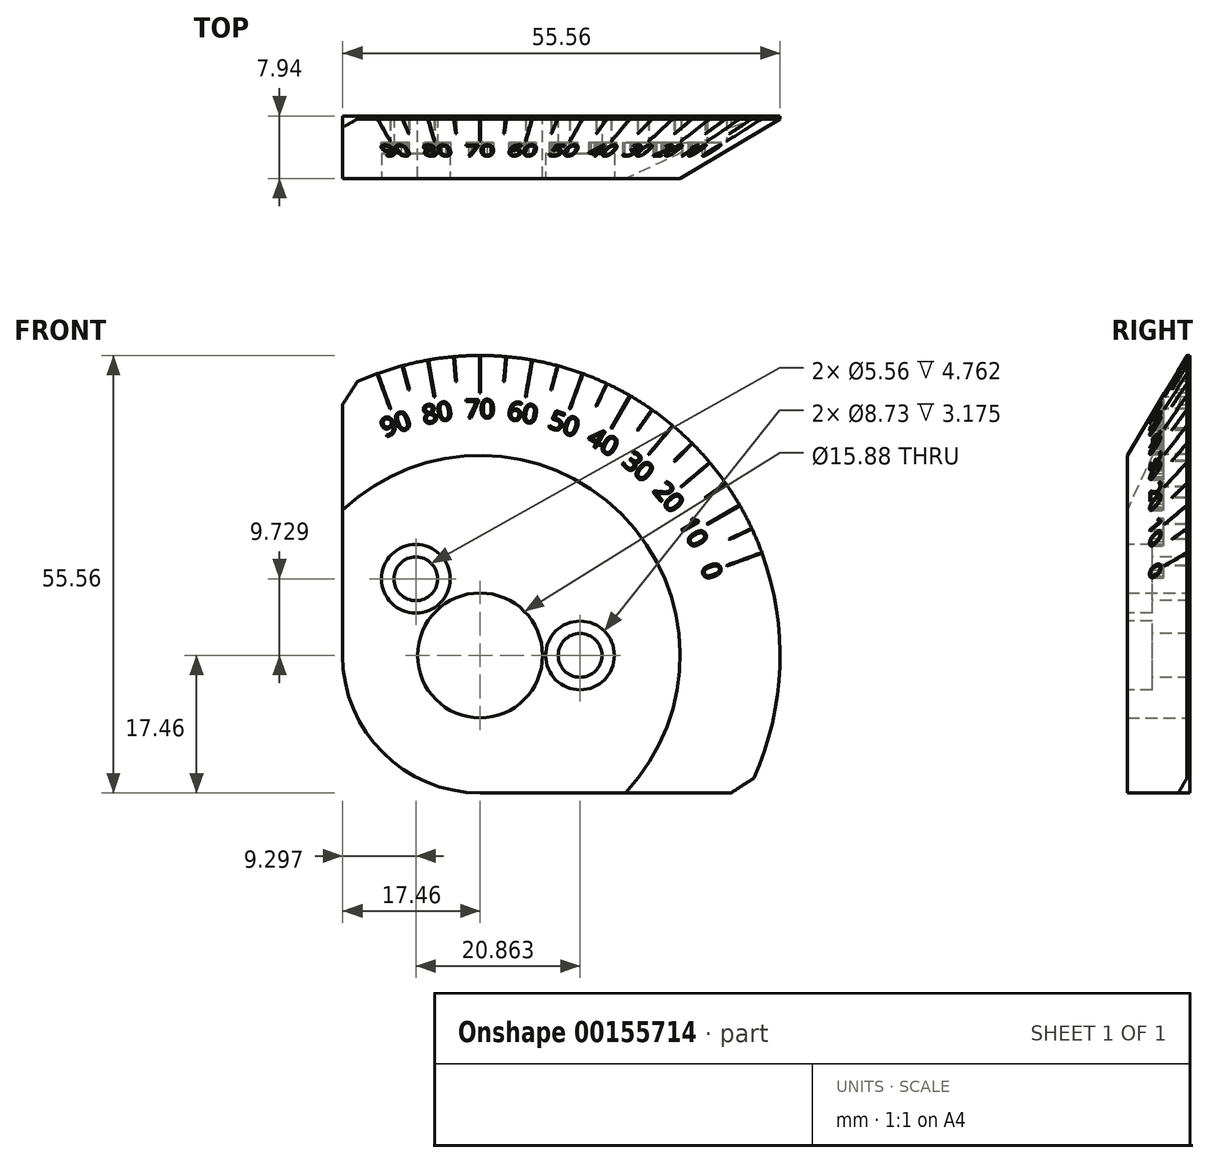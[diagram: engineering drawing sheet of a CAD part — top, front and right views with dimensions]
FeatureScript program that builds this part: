
annotation { "Feature Type Name" : "Feature", "Feature Type Description" : "" }
export const myFeature = defineFeature(function(context is Context, id is Id, definition is map)
    precondition{}
    {
        {
            var Q0;
            Q0=qCreatedBy(makeId("Front.planeOp"),FACE);
            var sketch = newSketch(context, id + "F0", { "sketchPlane" : qUnion([Q0])});
            skArc(sketch, "E0", {"start": v(33.86, -17.46) * mm, "mid": v(26.94, 26.94) * mm, "end": v(-17.46, 33.86) * mm});
            skArc(sketch, "E1", {"start": v(-17.46, 0) * mm, "mid": v(-12.35, -12.35) * mm, "end": v(0, -17.46) * mm});
            skCircle(sketch, "E2", {"center": v(0, 0) * mm, "radius": 7.94 * mm});
            skLineSegment(sketch, "E3", {"start": v(0, -17.46) * mm, "end": v(33.86, -17.46) * mm});
            skLineSegment(sketch, "E4", {"start": v(-17.46, 0) * mm, "end": v(-17.46, 33.86) * mm});
            skSolve(sketch);
        }
        {
            var Q0;
            Q0 = qSketchRegion(id + "F0", true);
            extrude(context, id + "F1", {"entities" : qUnion([Q0]), "endBound" : BoundingType.SYMMETRIC, "depth" : 7.94 * mm});
        }
        {
            var Q0;
            Q0=makeQuery(id+"F1.opExtrude","CAP_FACE",FACE,{"disambiguationData":[OSD([sQuery(id+"F0.wireOp",EDGE,"E0"),sQuery(id+"F0.wireOp",EDGE,"E1"),sQuery(id+"F0.wireOp",EDGE,"E2"),sQuery(id+"F0.wireOp",EDGE,"E3"),sQuery(id+"F0.wireOp",EDGE,"E4")])],"isStart":false});
            var sketch = newSketch(context, id + "F2", { "sketchPlane" : qUnion([Q0])});
            skLineSegment(sketch, "E5", {"start": v(0, 0) * mm, "end": v(38.1, 0) * mm, "construction": true});
            skArc(sketch, "E6", {"start": v(27.46, -17.46) * mm, "mid": v(23.01, 23.01) * mm, "end": v(-17.46, 27.46) * mm, "construction": true});
            skArc(sketch, "E7", {"start": v(28.4, -17.46) * mm, "mid": v(23.57, 23.57) * mm, "end": v(-17.46, 28.4) * mm, "construction": true});
            skArc(sketch, "E8", {"start": v(30.25, -17.46) * mm, "mid": v(24.7, 24.7) * mm, "end": v(-17.46, 30.25) * mm, "construction": true});
            skLineSegment(sketch, "E9", {"start": v(0, 0) * mm, "end": v(15.3, 5.57) * mm, "construction": true});
            skLineSegment(sketch, "E10.anchor1", {"start": v(0, 0) * mm, "end": v(0, 0) * mm});
            skLineSegment(sketch, "E10.anchor2", {"start": v(0, 0) * mm, "end": v(0, 0) * mm});
            skLineSegment(sketch, "E11.bottom", {"start": v(31.31, 11.45) * mm, "end": v(35.79, 13.08) * mm, "construction": true});
            skLineSegment(sketch, "E11.top", {"start": v(31.34, 11.36) * mm, "end": v(35.82, 12.98) * mm, "construction": true});
            skLineSegment(sketch, "E11.left", {"start": v(31.31, 11.45) * mm, "end": v(31.34, 11.36) * mm, "construction": true});
            skLineSegment(sketch, "E11.right", {"start": v(35.79, 13.08) * mm, "end": v(35.82, 12.98) * mm, "construction": true});
            skLineSegment(sketch, "E12", {"start": v(0, 0) * mm, "end": v(14.75, 6.88) * mm, "construction": true});
            skCircle(sketch, "E13", {"center": v(0, 0) * mm, "radius": 16.27 * mm, "construction": true});
            skPoint(sketch, "E14", {"position": v(15.3, 5.57) * mm});
            skLineSegment(sketch, "E15.bottom", {"start": v(31.63, 14.8) * mm, "end": v(34.5, 16.15) * mm, "construction": true});
            skLineSegment(sketch, "E15.top", {"start": v(31.67, 14.71) * mm, "end": v(34.55, 16.06) * mm, "construction": true});
            skLineSegment(sketch, "E15.left", {"start": v(31.63, 14.8) * mm, "end": v(31.67, 14.71) * mm, "construction": true});
            skLineSegment(sketch, "E15.right", {"start": v(34.5, 16.15) * mm, "end": v(34.55, 16.06) * mm, "construction": true});
            skLineSegment(sketch, "E16.8.8", {"start": v(0, 0) * mm, "end": v(-5.57, 15.3) * mm, "construction": true});
            skText(sketch, "E17", { "text": "90", "fontName": "OpenSans-Regular.ttf"});
            skText(sketch, "E18", { "text": "80", "fontName": "OpenSans-Regular.ttf"});
            skText(sketch, "E19", { "text": "70", "fontName": "OpenSans-Regular.ttf"});
            skText(sketch, "E20", { "text": "60", "fontName": "OpenSans-Regular.ttf"});
            skText(sketch, "E21", { "text": "30", "fontName": "OpenSans-Regular.ttf"});
            skText(sketch, "E22", { "text": "20", "fontName": "OpenSans-Regular.ttf"});
            skText(sketch, "E23", { "text": "10", "fontName": "OpenSans-Regular.ttf"});
            skText(sketch, "E24", { "text": "0", "fontName": "OpenSans-Regular.ttf"});
            skLineSegment(sketch, "E25", {"start": v(0, 0) * mm, "end": v(12.46, 10.46) * mm, "construction": true});
            skLineSegment(sketch, "E26", {"start": v(8.14, 14.1) * mm, "end": v(0, 0) * mm, "construction": true});
            skLineSegment(sketch, "E27", {"start": v(2.83, 16.02) * mm, "end": v(0, 0) * mm, "construction": true});
            skLineSegment(sketch, "E28", {"start": v(0, 0) * mm, "end": v(-2.83, 16.02) * mm, "construction": true});
            skLineSegment(sketch, "E29", {"start": v(0, 16.27) * mm, "end": v(0, 0) * mm, "construction": true});
            skLineSegment(sketch, "E30", {"start": v(5.57, 15.3) * mm, "end": v(0, 0) * mm, "construction": true});
            skLineSegment(sketch, "E31", {"start": v(0, 0) * mm, "end": v(10.46, 12.46) * mm, "construction": true});
            skLineSegment(sketch, "E32", {"start": v(14.1, 8.14) * mm, "end": v(0, 0) * mm, "construction": true});
            skText(sketch, "E33", { "text": "40", "fontName": "OpenSans-Regular.ttf"});
            skText(sketch, "E34", { "text": "50", "fontName": "OpenSans-Regular.ttf"});
            const initialGuessF2  = {"E17": [-0.01212, 0.02769, 0.9397, 0.34202, 0.00238], "E18": [-0.00712, 0.02937, 0.9848, 0.17365, 0.00238], "E19": [-0.00192, 0.03016, 1, 0, 0.00238], "E20": [0.00335, 0.03004, 0.9848, -0.17365, 0.00238], "E21": [0.01792, 0.02434, 0.76604, -0.64279, 0.00238], "E22": [0.02187, 0.02086, 0.64279, -0.76604, 0.00238], "E23": [0.02516, 0.01674, 0.5, -0.86603, 0.00238], "E24": [0.02801, 0.01123, 0.34202, -0.9397, 0.00238], "E33": [0.01342, 0.02708, 0.86603, -0.5, 0.00238], "E34": [0.00852, 0.029, 0.9397, -0.34202, 0.00238]};
            skSetInitialGuess(sketch, initialGuessF2);
            skSolve(sketch);
        }
        {
            var Q0;
            Q0=qCreatedBy(makeId("Right.planeOp"),FACE);
            var sketch = newSketch(context, id + "F3", { "sketchPlane" : qUnion([Q0])});
            skLineSegment(sketch, "E35", {"start": v(-3.97, 25.4) * mm, "end": v(-3.97, 38.1) * mm});
            skLineSegment(sketch, "E36", {"start": v(-3.97, 25.4) * mm, "end": v(3.59, 38.1) * mm});
            skLineSegment(sketch, "E37", {"start": v(-3.97, 38.1) * mm, "end": v(3.59, 38.1) * mm});
            skLineSegment(sketch, "E38", {"start": v(-13.9, 0) * mm, "end": v(49.7, 0) * mm, "construction": true});
            skSolve(sketch);
        }
        {
            var Q0;
            Q0 = qSketchRegion(id + "F3", true);
            var Q1;
            Q1=sQuery(id+"F3.wireOp",EDGE,"E38");
            revolve(context, id + "F4", {"operationType" : NewBodyOperationType.REMOVE, "entities" : qUnion([Q0]), "axis" : qUnion([Q1]), "revolveType" : RevolveType.FULL, "oppositeDirection" : true});
        }
        {
            var Q0;
            Q0 = qSketchRegion(id + "F2", true);
            extrude(context, id + "F5", {"entities" : qUnion([Q0]), "operationType" : NewBodyOperationType.REMOVE, "oppositeDirection" : true, "depth" : 4.57 * mm});
        }
        {
            var Q0;
            Q0=makeQuery(id+"F1.opExtrude","CAP_FACE",FACE,{"disambiguationData":[OSD([sQuery(id+"F0.wireOp",EDGE,"E0"),sQuery(id+"F0.wireOp",EDGE,"E1"),sQuery(id+"F0.wireOp",EDGE,"E2"),sQuery(id+"F0.wireOp",EDGE,"E3"),sQuery(id+"F0.wireOp",EDGE,"E4")])],"isStart":false});
            var sketch = newSketch(context, id + "F6", { "sketchPlane" : qUnion([Q0])});
            skLineSegment(sketch, "E39.0", {"start": v(31.31, 11.45) * mm, "end": v(31.34, 11.36) * mm});
            skLineSegment(sketch, "E40.0", {"start": v(31.31, 11.45) * mm, "end": v(35.79, 13.08) * mm});
            skLineSegment(sketch, "E41.0", {"start": v(31.34, 11.36) * mm, "end": v(35.82, 12.98) * mm});
            skLineSegment(sketch, "E42.0", {"start": v(35.79, 13.08) * mm, "end": v(35.82, 12.98) * mm});
            skLineSegment(sketch, "E43.0", {"start": v(31.63, 14.8) * mm, "end": v(34.5, 16.15) * mm});
            skLineSegment(sketch, "E44.0", {"start": v(31.67, 14.71) * mm, "end": v(34.55, 16.06) * mm});
            skLineSegment(sketch, "E45.0", {"start": v(31.63, 14.8) * mm, "end": v(31.67, 14.71) * mm});
            skLineSegment(sketch, "E46.0", {"start": v(34.5, 16.15) * mm, "end": v(34.55, 16.06) * mm});
            skLineSegment(sketch, "E47", {"start": v(0, 0) * mm, "end": v(6.88, 14.75) * mm, "construction": true});
            skLineSegment(sketch, "E48.0", {"start": v(28.85, 16.71) * mm, "end": v(28.9, 16.63) * mm});
            skLineSegment(sketch, "E49.0", {"start": v(28.9, 16.63) * mm, "end": v(33.02, 19) * mm});
            skLineSegment(sketch, "E50.0", {"start": v(28.85, 16.71) * mm, "end": v(32.97, 19.1) * mm});
            skLineSegment(sketch, "E51.0", {"start": v(32.97, 19.1) * mm, "end": v(33.02, 19) * mm});
            skLineSegment(sketch, "E52.1.0", {"start": v(25.5, 21.47) * mm, "end": v(29.15, 24.53) * mm});
            skLineSegment(sketch, "E52.1.1", {"start": v(25.57, 21.4) * mm, "end": v(29.22, 24.45) * mm});
            skLineSegment(sketch, "E52.1.4", {"start": v(28.58, 20.07) * mm, "end": v(31.18, 21.9) * mm});
            skLineSegment(sketch, "E52.1.5", {"start": v(28.64, 20) * mm, "end": v(31.24, 21.81) * mm});
            skLineSegment(sketch, "E52.1.6", {"start": v(29.15, 24.53) * mm, "end": v(29.22, 24.45) * mm});
            skLineSegment(sketch, "E52.1.7", {"start": v(25.5, 21.47) * mm, "end": v(25.57, 21.4) * mm});
            skLineSegment(sketch, "E52.1.9", {"start": v(28.58, 20.07) * mm, "end": v(28.64, 20) * mm});
            skLineSegment(sketch, "E52.1.10", {"start": v(31.18, 21.9) * mm, "end": v(31.24, 21.81) * mm});
            skLineSegment(sketch, "E52.2.0", {"start": v(21.4, 25.57) * mm, "end": v(24.45, 29.22) * mm});
            skLineSegment(sketch, "E52.2.1", {"start": v(21.47, 25.5) * mm, "end": v(24.53, 29.15) * mm});
            skLineSegment(sketch, "E52.2.2", {"start": v(25.5, 21.47) * mm, "end": v(29.15, 24.53) * mm});
            skLineSegment(sketch, "E52.2.3", {"start": v(25.57, 21.4) * mm, "end": v(29.22, 24.45) * mm});
            skLineSegment(sketch, "E52.2.4", {"start": v(24.66, 24.73) * mm, "end": v(26.9, 26.98) * mm});
            skLineSegment(sketch, "E52.2.5", {"start": v(24.73, 24.66) * mm, "end": v(26.98, 26.9) * mm});
            skLineSegment(sketch, "E52.2.6", {"start": v(24.45, 29.22) * mm, "end": v(24.53, 29.15) * mm});
            skLineSegment(sketch, "E52.2.7", {"start": v(21.4, 25.57) * mm, "end": v(21.47, 25.5) * mm});
            skLineSegment(sketch, "E52.2.8", {"start": v(29.15, 24.53) * mm, "end": v(29.22, 24.45) * mm});
            skLineSegment(sketch, "E52.2.9", {"start": v(24.66, 24.73) * mm, "end": v(24.73, 24.66) * mm});
            skLineSegment(sketch, "E52.2.10", {"start": v(26.9, 26.98) * mm, "end": v(26.98, 26.9) * mm});
            skLineSegment(sketch, "E52.2.11", {"start": v(25.5, 21.47) * mm, "end": v(25.57, 21.4) * mm});
            skLineSegment(sketch, "E52.3.0", {"start": v(16.63, 28.9) * mm, "end": v(19, 33.02) * mm});
            skLineSegment(sketch, "E52.3.1", {"start": v(16.71, 28.85) * mm, "end": v(19.1, 32.97) * mm});
            skLineSegment(sketch, "E52.3.2", {"start": v(21.4, 25.57) * mm, "end": v(24.45, 29.22) * mm});
            skLineSegment(sketch, "E52.3.3", {"start": v(21.47, 25.5) * mm, "end": v(24.53, 29.15) * mm});
            skLineSegment(sketch, "E52.3.4", {"start": v(20, 28.64) * mm, "end": v(21.81, 31.24) * mm});
            skLineSegment(sketch, "E52.3.5", {"start": v(20.07, 28.58) * mm, "end": v(21.9, 31.18) * mm});
            skLineSegment(sketch, "E52.3.6", {"start": v(19, 33.02) * mm, "end": v(19.1, 32.97) * mm});
            skLineSegment(sketch, "E52.3.7", {"start": v(16.63, 28.9) * mm, "end": v(16.71, 28.85) * mm});
            skLineSegment(sketch, "E52.3.8", {"start": v(24.45, 29.22) * mm, "end": v(24.53, 29.15) * mm});
            skLineSegment(sketch, "E52.3.9", {"start": v(20, 28.64) * mm, "end": v(20.07, 28.58) * mm});
            skLineSegment(sketch, "E52.3.10", {"start": v(21.81, 31.24) * mm, "end": v(21.9, 31.18) * mm});
            skLineSegment(sketch, "E52.3.11", {"start": v(21.4, 25.57) * mm, "end": v(21.47, 25.5) * mm});
            skLineSegment(sketch, "E52.4.0", {"start": v(11.36, 31.34) * mm, "end": v(12.98, 35.82) * mm});
            skLineSegment(sketch, "E52.4.1", {"start": v(11.45, 31.31) * mm, "end": v(13.08, 35.79) * mm});
            skLineSegment(sketch, "E52.4.2", {"start": v(16.63, 28.9) * mm, "end": v(19, 33.02) * mm});
            skLineSegment(sketch, "E52.4.3", {"start": v(16.71, 28.85) * mm, "end": v(19.1, 32.97) * mm});
            skLineSegment(sketch, "E52.4.4", {"start": v(14.71, 31.67) * mm, "end": v(16.06, 34.55) * mm});
            skLineSegment(sketch, "E52.4.5", {"start": v(14.8, 31.63) * mm, "end": v(16.15, 34.5) * mm});
            skLineSegment(sketch, "E52.4.6", {"start": v(12.98, 35.82) * mm, "end": v(13.08, 35.79) * mm});
            skLineSegment(sketch, "E52.4.7", {"start": v(11.36, 31.34) * mm, "end": v(11.45, 31.31) * mm});
            skLineSegment(sketch, "E52.4.8", {"start": v(19, 33.02) * mm, "end": v(19.1, 32.97) * mm});
            skLineSegment(sketch, "E52.4.9", {"start": v(14.71, 31.67) * mm, "end": v(14.8, 31.63) * mm});
            skLineSegment(sketch, "E52.4.10", {"start": v(16.06, 34.55) * mm, "end": v(16.15, 34.5) * mm});
            skLineSegment(sketch, "E52.4.11", {"start": v(16.63, 28.9) * mm, "end": v(16.71, 28.85) * mm});
            skLineSegment(sketch, "E52.5.0", {"start": v(5.74, 32.84) * mm, "end": v(6.57, 37.53) * mm});
            skLineSegment(sketch, "E52.5.1", {"start": v(5.84, 32.82) * mm, "end": v(6.66, 37.51) * mm});
            skLineSegment(sketch, "E52.5.2", {"start": v(11.36, 31.34) * mm, "end": v(12.98, 35.82) * mm});
            skLineSegment(sketch, "E52.5.3", {"start": v(11.45, 31.31) * mm, "end": v(13.08, 35.79) * mm});
            skLineSegment(sketch, "E52.5.4", {"start": v(9, 33.75) * mm, "end": v(9.81, 36.81) * mm});
            skLineSegment(sketch, "E52.5.5", {"start": v(9.09, 33.72) * mm, "end": v(9.9, 36.79) * mm});
            skLineSegment(sketch, "E52.5.6", {"start": v(6.57, 37.53) * mm, "end": v(6.66, 37.51) * mm});
            skLineSegment(sketch, "E52.5.7", {"start": v(5.74, 32.84) * mm, "end": v(5.84, 32.82) * mm});
            skLineSegment(sketch, "E52.5.8", {"start": v(12.98, 35.82) * mm, "end": v(13.08, 35.79) * mm});
            skLineSegment(sketch, "E52.5.9", {"start": v(9, 33.75) * mm, "end": v(9.09, 33.72) * mm});
            skLineSegment(sketch, "E52.5.10", {"start": v(9.81, 36.81) * mm, "end": v(9.9, 36.79) * mm});
            skLineSegment(sketch, "E52.5.11", {"start": v(11.36, 31.34) * mm, "end": v(11.45, 31.31) * mm});
            skLineSegment(sketch, "E52.6.0", {"start": v(-0.05, 33.34) * mm, "end": v(-0.05, 38.1) * mm});
            skLineSegment(sketch, "E52.6.1", {"start": v(0.05, 33.34) * mm, "end": v(0.05, 38.1) * mm});
            skLineSegment(sketch, "E52.6.2", {"start": v(5.74, 32.84) * mm, "end": v(6.57, 37.53) * mm});
            skLineSegment(sketch, "E52.6.3", {"start": v(5.84, 32.82) * mm, "end": v(6.66, 37.51) * mm});
            skLineSegment(sketch, "E52.6.4", {"start": v(3, 34.8) * mm, "end": v(3.27, 37.96) * mm});
            skLineSegment(sketch, "E52.6.5", {"start": v(3.1, 34.79) * mm, "end": v(3.37, 37.95) * mm});
            skLineSegment(sketch, "E52.6.6", {"start": v(-0.05, 38.1) * mm, "end": v(0.05, 38.1) * mm});
            skLineSegment(sketch, "E52.6.7", {"start": v(-0.05, 33.34) * mm, "end": v(0.05, 33.34) * mm});
            skLineSegment(sketch, "E52.6.8", {"start": v(6.57, 37.53) * mm, "end": v(6.66, 37.51) * mm});
            skLineSegment(sketch, "E52.6.9", {"start": v(3, 34.8) * mm, "end": v(3.1, 34.79) * mm});
            skLineSegment(sketch, "E52.6.10", {"start": v(3.27, 37.96) * mm, "end": v(3.37, 37.95) * mm});
            skLineSegment(sketch, "E52.6.11", {"start": v(5.74, 32.84) * mm, "end": v(5.84, 32.82) * mm});
            skLineSegment(sketch, "E52.7.0", {"start": v(-5.84, 32.82) * mm, "end": v(-6.66, 37.51) * mm});
            skLineSegment(sketch, "E52.7.1", {"start": v(-5.74, 32.84) * mm, "end": v(-6.57, 37.53) * mm});
            skLineSegment(sketch, "E52.7.2", {"start": v(-0.05, 33.34) * mm, "end": v(-0.05, 38.1) * mm});
            skLineSegment(sketch, "E52.7.3", {"start": v(0.05, 33.34) * mm, "end": v(0.05, 38.1) * mm});
            skLineSegment(sketch, "E52.7.4", {"start": v(-3.1, 34.79) * mm, "end": v(-3.37, 37.95) * mm});
            skLineSegment(sketch, "E52.7.5", {"start": v(-3, 34.8) * mm, "end": v(-3.27, 37.96) * mm});
            skLineSegment(sketch, "E52.7.6", {"start": v(-6.66, 37.51) * mm, "end": v(-6.57, 37.53) * mm});
            skLineSegment(sketch, "E52.7.7", {"start": v(-5.84, 32.82) * mm, "end": v(-5.74, 32.84) * mm});
            skLineSegment(sketch, "E52.7.8", {"start": v(-0.05, 38.1) * mm, "end": v(0.05, 38.1) * mm});
            skLineSegment(sketch, "E52.7.9", {"start": v(-3.1, 34.79) * mm, "end": v(-3, 34.8) * mm});
            skLineSegment(sketch, "E52.7.10", {"start": v(-3.37, 37.95) * mm, "end": v(-3.27, 37.96) * mm});
            skLineSegment(sketch, "E52.7.11", {"start": v(-0.05, 33.34) * mm, "end": v(0.05, 33.34) * mm});
            skLineSegment(sketch, "E52.8.0", {"start": v(-11.45, 31.31) * mm, "end": v(-13.08, 35.79) * mm});
            skLineSegment(sketch, "E52.8.1", {"start": v(-11.36, 31.34) * mm, "end": v(-12.98, 35.82) * mm});
            skLineSegment(sketch, "E52.8.2", {"start": v(-5.84, 32.82) * mm, "end": v(-6.66, 37.51) * mm});
            skLineSegment(sketch, "E52.8.3", {"start": v(-5.74, 32.84) * mm, "end": v(-6.57, 37.53) * mm});
            skLineSegment(sketch, "E52.8.4", {"start": v(-9.09, 33.72) * mm, "end": v(-9.9, 36.79) * mm});
            skLineSegment(sketch, "E52.8.5", {"start": v(-9, 33.75) * mm, "end": v(-9.81, 36.81) * mm});
            skLineSegment(sketch, "E52.8.6", {"start": v(-13.08, 35.79) * mm, "end": v(-12.98, 35.82) * mm});
            skLineSegment(sketch, "E52.8.7", {"start": v(-11.45, 31.31) * mm, "end": v(-11.36, 31.34) * mm});
            skLineSegment(sketch, "E52.8.8", {"start": v(-6.66, 37.51) * mm, "end": v(-6.57, 37.53) * mm});
            skLineSegment(sketch, "E52.8.9", {"start": v(-9.09, 33.72) * mm, "end": v(-9, 33.75) * mm});
            skLineSegment(sketch, "E52.8.10", {"start": v(-9.9, 36.79) * mm, "end": v(-9.81, 36.81) * mm});
            skLineSegment(sketch, "E52.8.11", {"start": v(-5.84, 32.82) * mm, "end": v(-5.74, 32.84) * mm});
            skPoint(sketch, "E52.center", {"position": v(0, 0) * mm});
            skLineSegment(sketch, "E52.anchor1", {"start": v(0, 0) * mm, "end": v(31.34, 11.36) * mm, "construction": true});
            skLineSegment(sketch, "E52.anchor2", {"start": v(0, 0) * mm, "end": v(-5.74, 32.84) * mm, "construction": true});
            skSolve(sketch);
        }
        {
            var Q0;
            Q0 = qSketchRegion(id + "F6", true);
            extrude(context, id + "F7", {"entities" : qUnion([Q0]), "operationType" : NewBodyOperationType.REMOVE, "oppositeDirection" : true, "depth" : 7.56 * mm});
        }
        {
            var Q0;
            Q0=makeQuery(id+"F1.opExtrude","SWEPT_EDGE",EDGE,{"disambiguationData":[OSD([sQuery(id+"F0.wireOp",EDGE,"E0"),sQuery(id+"F0.wireOp",EDGE,"E4")])]});
            var Q1;
            Q1=makeQuery(id+"F1.opExtrude","SWEPT_EDGE",EDGE,{"disambiguationData":[OSD([sQuery(id+"F0.wireOp",EDGE,"E0"),sQuery(id+"F0.wireOp",EDGE,"E3")])]});
            chamfer(context, id + "F8", {"entities" : qUnion([Q0, Q1]), "width" : 3.17 * mm, "tangentPropagation" : true});
        }
        {
            var Q0;
            Q0=makeQuery(id+"F1.opExtrude","CAP_FACE",FACE,{"disambiguationData":[OSD([sQuery(id+"F0.wireOp",EDGE,"E0"),sQuery(id+"F0.wireOp",EDGE,"E1"),sQuery(id+"F0.wireOp",EDGE,"E2"),sQuery(id+"F0.wireOp",EDGE,"E3"),sQuery(id+"F0.wireOp",EDGE,"E4")])],"isStart":false});
            var sketch = newSketch(context, id + "F9", { "sketchPlane" : qUnion([Q0])});
            skCircle(sketch, "E53", {"center": v(0, 0) * mm, "radius": 12.7 * mm, "construction": true});
            skLineSegment(sketch, "E54", {"start": v(0, 0) * mm, "end": v(12.7, 0) * mm, "construction": true});
            skLineSegment(sketch, "E55", {"start": v(0, 0) * mm, "end": v(-8.16, 9.73) * mm, "construction": true});
            skSolve(sketch);
        }
        {
            var Q0;
            Q0=sQuery(id+"F9.wireOp",VERTEX,"E54.end");
            var Q1;
            Q1=sQuery(id+"F9.wireOp",VERTEX,"E55.end");
            var Q2;
            Q2=makeQuery(id+"F1.opExtrude","SWEPT_BODY",BODY,{"disambiguationData":[OSD([sQuery(id+"F0.wireOp",EDGE,"E0"),sQuery(id+"F0.wireOp",EDGE,"E1"),sQuery(id+"F0.wireOp",EDGE,"E2"),sQuery(id+"F0.wireOp",EDGE,"E3"),sQuery(id+"F0.wireOp",EDGE,"E4")])]});
            hole(context, id + "F10", {"style" : HoleStyle.C_BORE, "endStyle" : HoleEndStyle.THROUGH, "holeDiameter" : 5.56 * mm, "cBoreDiameter" : 8.73 * mm, "cBoreDepth" : 3.17 * mm, "startFromSketch" : true, "locations" : qUnion([Q0, Q1]), "scope" : qUnion([Q2]), "isTappedThrough" : true});
        }
    });
